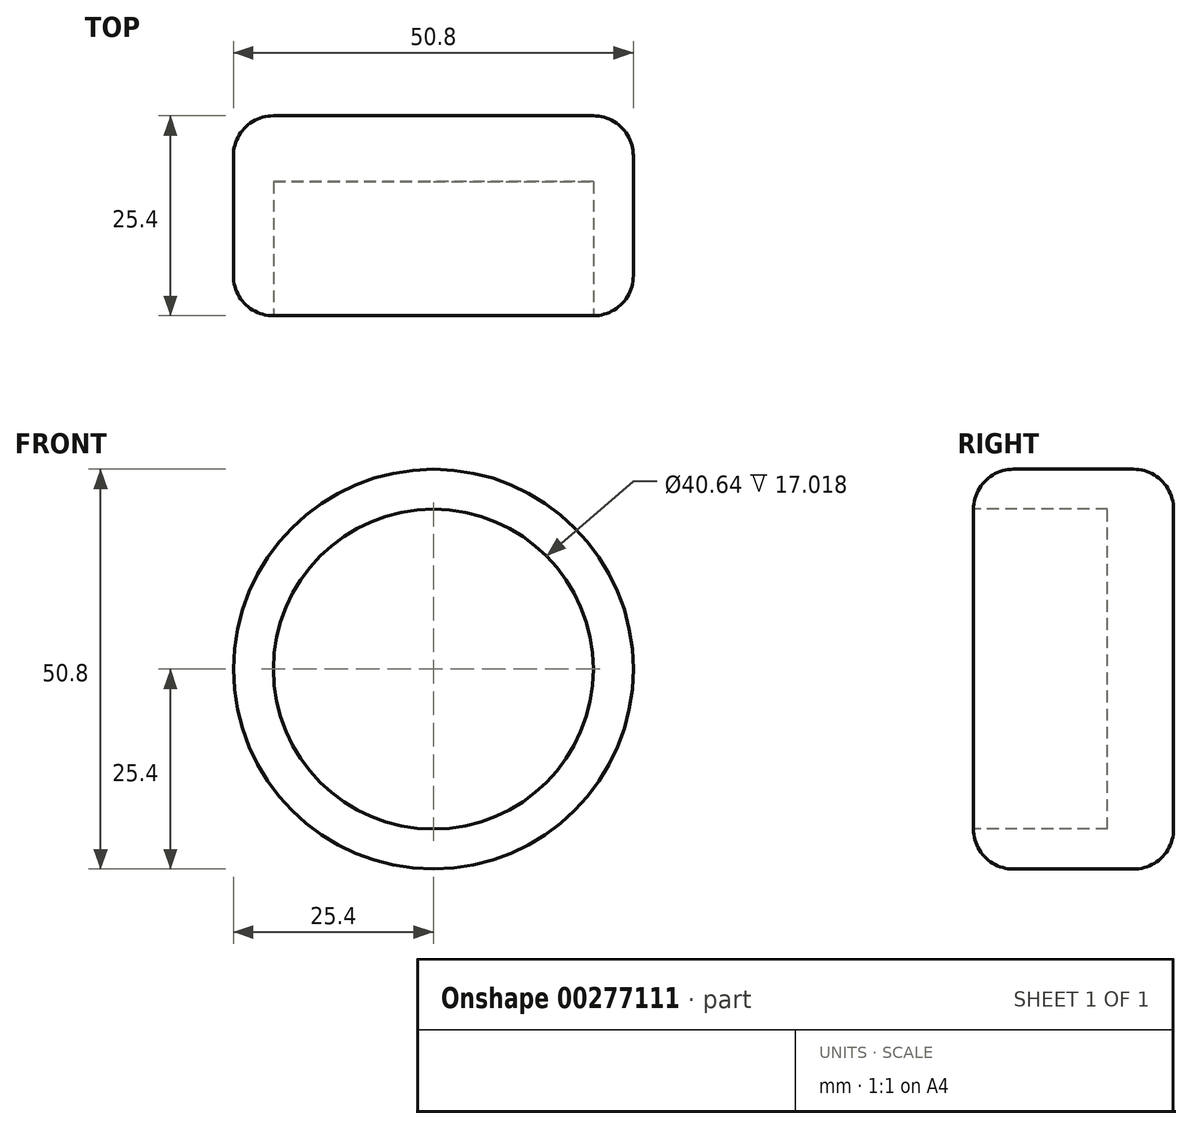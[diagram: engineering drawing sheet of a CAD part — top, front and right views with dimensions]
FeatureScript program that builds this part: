
annotation { "Feature Type Name" : "Feature", "Feature Type Description" : "" }
export const myFeature = defineFeature(function(context is Context, id is Id, definition is map)
    precondition{}
    {
        {
            var Q0;
            Q0=qCreatedBy(makeId("Front.planeOp"),FACE);
            var sketch = newSketch(context, id + "F0", { "sketchPlane" : qUnion([Q0])});
            skCircle(sketch, "E0", {"center": v(0, 0) * mm, "radius": 25.4 * mm});
            skSolve(sketch);
        }
        {
            var Q0;
            Q0 = qSketchRegion(id + "F0", true);
            extrude(context, id + "F1", {"entities" : qUnion([Q0]), "depth" : 25.4 * mm});
        }
        {
            var Q0;
            Q0=makeQuery(id+"F1.opExtrude","SWEPT_FACE",FACE,{"disambiguationData":[OSD([sQuery(id+"F0.wireOp",EDGE,"E0")])]});
            fillet(context, id + "F2", {"entities" : qUnion([Q0]), "radius" : 5.08 * mm, "tangentPropagation" : true, "allowEdgeOverflow" : false});
        }
        {
            var Q0;
            Q0=makeQuery(id+"F1.opExtrude","CAP_FACE",FACE,{"disambiguationData":[OSD([sQuery(id+"F0.wireOp",EDGE,"E0")])],"isStart":false});
            extrude(context, id + "F3", {"entities" : qUnion([Q0]), "operationType" : NewBodyOperationType.REMOVE, "oppositeDirection" : true, "depth" : 17.02 * mm});
        }
    });
